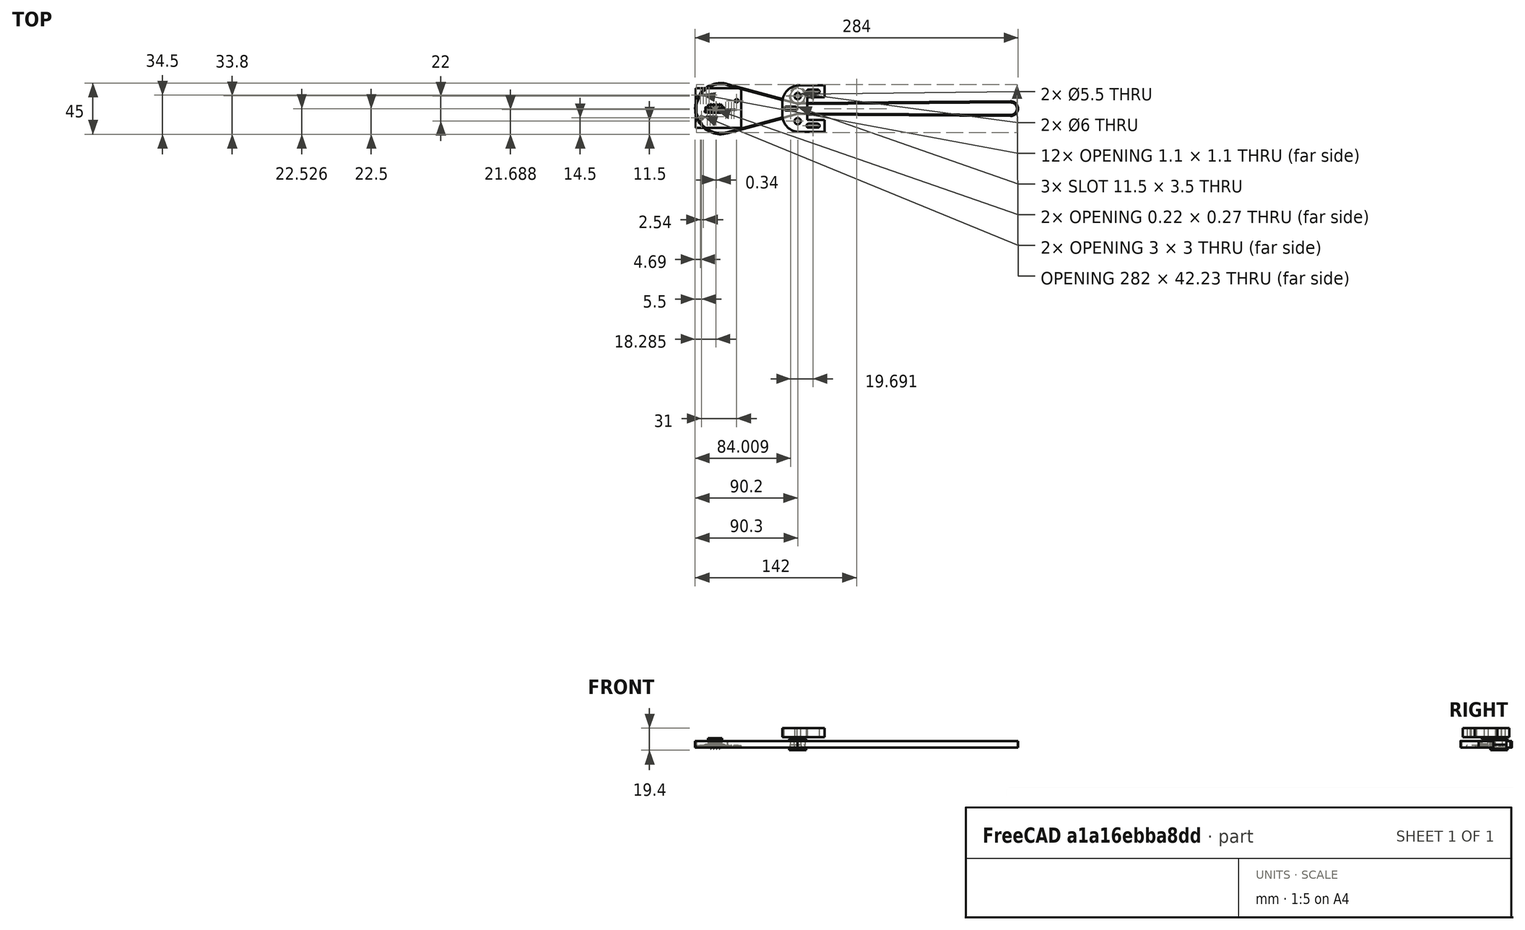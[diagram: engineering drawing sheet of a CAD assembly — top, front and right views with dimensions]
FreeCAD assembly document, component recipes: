
FREECAD ASSEMBLY — COMPONENT RECIPES ("GT2_80")

This assembly document has 18 components, labeled P0..P17 below (a component is one placed body or linked part). 13 of them carry a construction recipe — the FreeCAD feature program that regenerates the part from scratch, quoted from this document or its linked companion documents; the rest are supplied as boundary geometry only. No exploded tour is included for this assembly.
NOTE — document 2 of 2 of this assembly tour. The two overview renders and the header above are repeated from document 1; the component sections below continue where the previous document stopped.
COMPONENT P11 — recipe-attached ("GearHolderFullLength001", modeled in this document).
Construction recipe (the document's own serialized feature program — sketch geometry with constraints, then the solid features built on it; lengths are millimeters unless a unit is written):

FEATURE [PartDesign::ShapeBinder] CopyPocket001
  TraceSupport = false
FEATURE [Sketcher::SketchObject] Sketch079
  ArcFitTolerance = 1e-06
  AttachmentSupport = -> [CopyPocket001]
  FullyConstrained = true
  MakeInternals = false
  MapMode = 5
  Placement = pos=(0,0,19.5) rot=(0,0,1;0rad)
  expr: Constraints[1] = <<Spreadsheet001>>.TopDiameter
  sketch-geometry (1):
    g0: Circle CenterX=0 CenterY=0 CenterZ=0 NormalX=0 NormalY=0 NormalZ=1 AngleXU=0 Radius=32
  constraints (2):
    c: Coincident(g0,g-1)
    c: Diameter(g0) = 64
FEATURE [PartDesign::Pad] Pad033
  Direction = (0,0,1)
  Length = 37
  Length2 = 10
  Profile = -> Sketch079
  ReferenceAxis = -> Sketch079 [N_Axis]
  Refine = true
  Reversed = true
  Suppressed = false
  Type = 0
  expr: Length = <<Spreadsheet001>>.SecondArmHeight
FEATURE [Sketcher::SketchObject] Sketch080
  ArcFitTolerance = 1e-06
  AttachmentSupport = -> [Pad033]
  FullyConstrained = true
  MakeInternals = false
  MapMode = 5
  Placement = pos=(0,0,-17.5) rot=(1,0,0;3.14159rad)
  expr: Constraints[1] = <<Spreadsheet001>>.TopBearingDiameter
  sketch-geometry (1):
    g0: Circle CenterX=0 CenterY=0 CenterZ=0 NormalX=0 NormalY=0 NormalZ=1 AngleXU=0 Radius=18.5
  constraints (2):
    c: Coincident(g0,g-1)
    c: Diameter(g0) = 37
FEATURE [PartDesign::Pocket] Pocket032
  BaseFeature = -> Pad033
  Direction = (0,0,1)
  Length = 35
  Length2 = 5
  Profile = -> Sketch080
  ReferenceAxis = -> Sketch080 [N_Axis]
  Refine = true
  Suppressed = false
  Type = 0
  expr: Length = <<Spreadsheet001>>.SecondArmHeight - <<Spreadsheet001>>.TopThickness
FEATURE [Sketcher::SketchObject] Sketch081
  ArcFitTolerance = 1e-06
  AttachmentSupport = -> [Pocket032]
  FullyConstrained = true
  MakeInternals = false
  MapMode = 5
  Placement = pos=(0,0,-17.5) rot=(1,0,0;3.14159rad)
  expr: Constraints[1] = <<Spreadsheet001>>.TopThrustBearingDiameter + 6
  sketch-geometry (1):
    g0: Circle CenterX=0 CenterY=0 CenterZ=0 NormalX=0 NormalY=0 NormalZ=1 AngleXU=0 Radius=26.5
  constraints (2):
    c: Coincident(g0,g-1)
    c: Diameter(g0) = 53
FEATURE [PartDesign::Pocket] Pocket033
  BaseFeature = -> Pocket032
  Direction = (0,0,1)
  Length = 27
  Length2 = 5
  Profile = -> Sketch081
  ReferenceAxis = -> Sketch081 [N_Axis]
  Refine = true
  Suppressed = false
  Type = 0
  expr: Length = <<Spreadsheet001>>.SecondArmHeight - <<Spreadsheet001>>.TopThickness - <<Spreadsheet001>>.TopBearingHeight
FEATURE [Sketcher::SketchObject] Sketch082
  ArcFitTolerance = 1e-06
  AttachmentSupport = -> [Pocket033]
  FullyConstrained = true
  MakeInternals = false
  MapMode = 5
  Placement = pos=(0,0,19.5) rot=(0,0,1;0rad)
  expr: Constraints[1] = <<Spreadsheet001>>.TopBearingHole + 6
  sketch-geometry (1):
    g0: Circle CenterX=0 CenterY=0 CenterZ=0 NormalX=0 NormalY=0 NormalZ=1 AngleXU=0 Radius=15.5
  constraints (2):
    c: Coincident(g0,g-1)
    c: Diameter(g0) = 31
FEATURE [PartDesign::Pocket] Pocket034
  BaseFeature = -> Pocket033
  Direction = (0,0,-1)
  Length = 5
  Length2 = 5
  Profile = -> Sketch082
  ReferenceAxis = -> Sketch082 [N_Axis]
  Refine = true
  Suppressed = false
  Type = 1
FEATURE [Sketcher::SketchObject] Sketch083
  ArcFitTolerance = 1e-06
  AttachmentSupport = -> [Pocket034]
  FullyConstrained = false
  MakeInternals = false
  MapMode = 5
  Placement = pos=(0,0,19.5) rot=(0,0,1;0rad)
  expr: Constraints[1] = <<Spreadsheet001>>.TopDiameter
  expr: Constraints[7] = (<<Spreadsheet001>>.TopFaceWidth + 4) / 2
  sketch-geometry (5):
    g0: ArcOfCircle CenterX=0 CenterY=0 CenterZ=0 NormalX=0 NormalY=0 NormalZ=1 AngleXU=0 Radius=32 StartAngle=2.13736 EndAngle=4.14582
    g1: LineSegment StartX=-17.1756 StartY=27 StartZ=0 EndX=-230.439 EndY=27 EndZ=0
    g2: LineSegment StartX=-230.439 StartY=-27 StartZ=0 EndX=-17.1756 EndY=-27 EndZ=0
    g3: GeomPoint [constr] X=0 Y=0 Z=0
    g4: ArcOfCircle CenterX=-255 CenterY=0 CenterZ=0 NormalX=0 NormalY=0 NormalZ=1 AngleXU=0 Radius=36.5 StartAngle=0.832663 EndAngle=5.45052
  constraints (13):
    c: Coincident(g0,g-1)
    c: Diameter(g0) = 64
    c: Horizontal(g1)
    c: Horizontal(g2)
    c: Coincident(g3,g0)
    c: Coincident(g1,g0)
    c: Coincident(g2,g0)
    c: Distance(g-1,g1) = 27
    c: PointOnObject(g4,g-1)
    c: Diameter(g4) = 73
    c: DistanceX(g4,g-1) = 255
    c: Coincident(g4,g2)
    c: Coincident(g4,g1)
FEATURE [PartDesign::Pad] Pad034
  BaseFeature = -> Pocket034
  Direction = (0,0,1)
  Length = 37
  Length2 = 10
  Profile = -> Sketch083
  ReferenceAxis = -> Sketch083 [N_Axis]
  Refine = true
  Reversed = true
  Suppressed = false
  Type = 0
  expr: Length = <<Spreadsheet001>>.SecondArmHeight
FEATURE [Sketcher::SketchObject] Sketch084
  ArcFitTolerance = 1e-06
  AttachmentSupport = -> [Pad034]
  ExternalGeometry = -> [Pad034]
  FullyConstrained = false
  MakeInternals = false
  MapMode = 5
  Placement = pos=(0,0,-17.5) rot=(1,0,0;3.14159rad)
  sketch-geometry (6):
    g0: LineSegment StartX=-219.873 StartY=-22 StartZ=0 EndX=-6.4835 EndY=-22 EndZ=0
    g1: LineSegment StartX=-6.4835 StartY=-22 StartZ=0 EndX=-6.4835 EndY=22 EndZ=0
    g2: LineSegment StartX=-6.4835 StartY=22 StartZ=0 EndX=-219.873 EndY=22 EndZ=0
    g3: LineSegment StartX=-219.873 StartY=22 StartZ=0 EndX=-229.114 EndY=15 EndZ=0
    g4: LineSegment StartX=-229.114 StartY=-15 StartZ=0 EndX=-219.873 EndY=-22 EndZ=0
    g5: LineSegment StartX=-229.114 StartY=15 StartZ=0 EndX=-229.114 EndY=-15 EndZ=0
  constraints (14):
    c: Coincident(g0,g1)
    c: Coincident(g1,g2)
    c: Vertical(g1)
    c: Horizontal(g0)
    c: Horizontal(g2)
    c: Distance(g2,g-3) = 5
    c: Distance(g-4,g0) = 5
    c: Coincident(g3,g2)
    c: Coincident(g4,g0)
    c: Vertical(g5)
    c: Coincident(g5,g3)
    c: Coincident(g5,g4)
    c: Distance(g3,g-1) = 15
    c: Distance(g4,g-1) = 15
FEATURE [PartDesign::Pocket] Pocket035
  BaseFeature = -> Pad034
  Direction = (0,0,1)
  Length = 32
  Length2 = 5
  Profile = -> Sketch084
  ReferenceAxis = -> Sketch084 [N_Axis]
  Refine = true
  Suppressed = false
  Type = 0
FEATURE [Sketcher::SketchObject] Sketch085
  ArcFitTolerance = 1e-06
  AttachmentOffset = pos=(0,0,-49) rot=(0,0,1;0rad)
  AttachmentSupport = -> [YZ_Plane015]
  ExternalGeometry = -> [Pocket035]
  FullyConstrained = true
  MakeInternals = false
  MapMode = 5
  Placement = pos=(-49,0,0) rot=(0.57735,0.57735,0.57735;2.0944rad)
  sketch-geometry (5):
    g0: LineSegment StartX=22 StartY=14.5 StartZ=0 EndX=5 EndY=14.5 EndZ=0
    g1: LineSegment StartX=16 StartY=-17.5 StartZ=0 EndX=22 EndY=-17.5 EndZ=0
    g2: LineSegment StartX=22 StartY=-17.5 StartZ=0 EndX=22 EndY=14.5 EndZ=0
    g3: LineSegment StartX=16 StartY=3.5 StartZ=0 EndX=16 EndY=-17.5 EndZ=0
    g4: LineSegment StartX=16 StartY=3.5 StartZ=0 EndX=5 EndY=14.5 EndZ=0
  constraints (13):
    c: Coincident(g-4,g0)
    c: PointOnObject(g1,g-3)
    c: Coincident(g1,g-4)
    c: Coincident(g1,g2)
    c: Coincident(g2,g0)
    c: DistanceX(g1,g1) = 6
    c: Horizontal(g0)
    c: Coincident(g3,g1)
    c: Vertical(g3)
    c: Coincident(g3,g4)
    c: Angle(g4,g3) = 2.35619
    c: DistanceY(g3,g3) = 21
    c: Coincident(g0,g4)
FEATURE [PartDesign::Pad] Pad035
  BaseFeature = -> Pocket035
  Direction = (1,0,0)
  Length = 2
  Length2 = 10
  Profile = -> Sketch085
  ReferenceAxis = -> Sketch085 [N_Axis]
  Refine = true
  Suppressed = false
  Type = 0
FEATURE [PartDesign::Mirrored] Mirrored
  MirrorPlane = -> Sketch085 [V_Axis]
  Refine = true
  Suppressed = false
  TransformMode = 0
FEATURE [PartDesign::LinearPattern] LinearPattern
  Direction = -> X_Axis015
  Length = 150
  Mode = 1
  Occurrences = 4
  Offset = 50
  Refine = true
  Reversed = true
  Suppressed = false
  TransformMode = 0
FEATURE [Sketcher::SketchObject] Sketch086
  ArcFitTolerance = 1e-06
  AttachmentSupport = -> [Pad035]
  ExternalGeometry = -> [Pad035]
  FullyConstrained = true
  MakeInternals = false
  MapMode = 5
  Placement = pos=(0,0,14.5) rot=(1,0,0;3.14159rad)
  sketch-geometry (1):
    g0: Circle CenterX=-48 CenterY=-22 CenterZ=0 NormalX=0 NormalY=0 NormalZ=1 AngleXU=0 Radius=4
  constraints (3):
    c: Diameter(g0) = 8
    c: Horizontal(g0,g-3)
    c: Distance(g0,g-3) = 1
FEATURE [PartDesign::Pad] Pad036
  BaseFeature = -> Pad035
  Direction = (0,0,-1)
  Length = 32
  Length2 = 10
  Profile = -> Sketch086
  ReferenceAxis = -> Sketch086 [N_Axis]
  Refine = true
  Suppressed = false
  Type = 0
FEATURE [Sketcher::SketchObject] Sketch087
  ArcFitTolerance = 1e-06
  AttachmentSupport = -> [Pad036]
  ExternalGeometry = -> [Pad036]
  FullyConstrained = true
  MakeInternals = false
  MapMode = 5
  Placement = pos=(0,0,-17.5) rot=(1,0,0;3.14159rad)
  sketch-geometry (1):
    g0: Circle CenterX=-48 CenterY=-22 CenterZ=0 NormalX=0 NormalY=0 NormalZ=1 AngleXU=0 Radius=2
  constraints (2):
    c: Diameter(g0) = 4
    c: Coincident(g0,g-3)
FEATURE [PartDesign::Pocket] Pocket036
  BaseFeature = -> Pad036
  Direction = (0,0,1)
  Length = 10
  Length2 = 5
  Profile = -> Sketch087
  ReferenceAxis = -> Sketch087 [N_Axis]
  Refine = true
  Suppressed = false
  Type = 0
FEATURE [PartDesign::MultiTransform] MultiTransform
  BaseFeature = -> Pocket036
  Originals = -> [Pad035,Pad036,Pocket036]
  Refine = true
  Suppressed = false
  TransformMode = 0
  Transformations = -> [Mirrored,LinearPattern]
FEATURE [Sketcher::SketchObject] Sketch088
  ArcFitTolerance = 1e-06
  AttachmentSupport = -> [Pocket035]
  ExternalGeometry = -> [Pocket035]
  FullyConstrained = false
  MakeInternals = false
  MapMode = 5
  Placement = pos=(0,0,-17.5) rot=(1,0,0;3.14159rad)
  sketch-geometry (8):
    g0: ArcOfCircle CenterX=-270.556 CenterY=15.5564 CenterZ=0 NormalX=0 NormalY=0 NormalZ=1 AngleXU=0 Radius=6 StartAngle=0.785398 EndAngle=3.92699
    g1: ArcOfCircle CenterX=-239.444 CenterY=15.5563 CenterZ=0 NormalX=0 NormalY=0 NormalZ=1 AngleXU=0 Radius=6 StartAngle=5.49779 EndAngle=8.63938
    g2: ArcOfCircle CenterX=-270.556 CenterY=-15.5564 CenterZ=0 NormalX=0 NormalY=0 NormalZ=1 AngleXU=0 Radius=6 StartAngle=2.35619 EndAngle=5.49779
    g3: ArcOfCircle CenterX=-239.444 CenterY=-15.5563 CenterZ=0 NormalX=0 NormalY=0 NormalZ=1 AngleXU=0 Radius=6 StartAngle=3.92699 EndAngle=7.06858
    g4: ArcOfCircle CenterX=-255 CenterY=0 CenterZ=0 NormalX=0 NormalY=0 NormalZ=1 AngleXU=0 Radius=22.8035 StartAngle=2.62245 EndAngle=3.66074
    g5: ArcOfCircle CenterX=-255 CenterY=0 CenterZ=0 NormalX=0 NormalY=0 NormalZ=1 AngleXU=0 Radius=22.8035 StartAngle=1.05165 EndAngle=2.08994
    g6: ArcOfCircle CenterX=-255 CenterY=0 CenterZ=0 NormalX=0 NormalY=0 NormalZ=1 AngleXU=0 Radius=22.8035 StartAngle=5.76404 EndAngle=6.80233
    g7: ArcOfCircle CenterX=-255 CenterY=0 CenterZ=0 NormalX=0 NormalY=0 NormalZ=1 AngleXU=0 Radius=22.8035 StartAngle=4.19324 EndAngle=5.23154
  constraints (14):
    c: Coincident(g5,g0)
    c: Coincident(g4,g0)
    c: Equal(g4,g5)
    c: Coincident(g4,g5)
    c: Equal(g4,g6)
    c: Coincident(g4,g6)
    c: Coincident(g1,g5)
    c: Coincident(g1,g6)
    c: Coincident(g3,g6)
    c: Coincident(g3,g7)
    c: Equal(g4,g7)
    c: Coincident(g4,g7)
    c: Coincident(g2,g4)
    c: Coincident(g2,g7)
FEATURE [PartDesign::Pocket] Pocket037
  BaseFeature = -> MultiTransform
  Direction = (0,0,1)
  Length = 27
  Length2 = 5
  Profile = -> Sketch088
  ReferenceAxis = -> Sketch088 [N_Axis]
  Refine = true
  Suppressed = false
  Type = 0
FEATURE [Sketcher::SketchObject] Sketch089
  ArcFitTolerance = 1e-06
  AttachmentSupport = -> [Pad034]
  ExternalGeometry = -> [Pad034]
  FullyConstrained = true
  MakeInternals = false
  MapMode = 5
  Placement = pos=(0,0,19.5) rot=(0,0,1;0rad)
  sketch-geometry (5):
    g0: LineSegment StartX=-277 StartY=-22 StartZ=0 EndX=-233 EndY=-22 EndZ=0
    g1: LineSegment StartX=-233 StartY=-22 StartZ=0 EndX=-233 EndY=22 EndZ=0
    g2: LineSegment StartX=-233 StartY=22 StartZ=0 EndX=-277 EndY=22 EndZ=0
    g3: LineSegment StartX=-277 StartY=22 StartZ=0 EndX=-277 EndY=-22 EndZ=0
    g4: GeomPoint [constr] X=-255 Y=0 Z=0
  constraints (12):
    c: Coincident(g0,g1)
    c: Coincident(g1,g2)
    c: Coincident(g2,g3)
    c: Coincident(g3,g0)
    c: Horizontal(g0)
    c: Horizontal(g2)
    c: Vertical(g1)
    c: Vertical(g3)
    c: Symmetric(g2,g0,g4)
    c: Distance(g1,g3) = 44
    c: Distance(g0,g2) = 44
    c: Coincident(g4,g-3)
FEATURE [PartDesign::Pocket] Pocket038
  BaseFeature = -> Pocket037
  Direction = (0,0,-1)
  Length = 7
  Length2 = 5
  Profile = -> Sketch089
  ReferenceAxis = -> Sketch089 [N_Axis]
  Refine = true
  Suppressed = false
  Type = 0
FEATURE [Sketcher::SketchObject] Sketch090
  ArcFitTolerance = 1e-06
  AttachmentSupport = -> [Pad034]
  ExternalGeometry = -> [Pad034]
  FullyConstrained = true
  MakeInternals = false
  MapMode = 5
  Placement = pos=(0,0,19.5) rot=(0,0,1;0rad)
  sketch-geometry (16):
    g0: ArcOfCircle CenterX=-271.5 CenterY=15.5 CenterZ=0 NormalX=0 NormalY=0 NormalZ=1 AngleXU=0 Radius=1.5 StartAngle=1.5708 EndAngle=4.71239
    g1: ArcOfCircle CenterX=-269.5 CenterY=15.5 CenterZ=0 NormalX=0 NormalY=0 NormalZ=1 AngleXU=0 Radius=1.5 StartAngle=4.71239 EndAngle=7.85398
    g2: LineSegment StartX=-271.5 StartY=17 StartZ=0 EndX=-269.5 EndY=17 EndZ=0
    g3: LineSegment StartX=-271.5 StartY=14 StartZ=0 EndX=-269.5 EndY=14 EndZ=0
    g4: ArcOfCircle CenterX=-240.5 CenterY=15.5 CenterZ=0 NormalX=0 NormalY=0 NormalZ=1 AngleXU=0 Radius=1.5 StartAngle=1.5708 EndAngle=4.71239
    g5: ArcOfCircle CenterX=-238.5 CenterY=15.5 CenterZ=0 NormalX=0 NormalY=0 NormalZ=1 AngleXU=0 Radius=1.5 StartAngle=4.71239 EndAngle=7.85398
    g6: LineSegment StartX=-240.5 StartY=17 StartZ=0 EndX=-238.5 EndY=17 EndZ=0
    g7: LineSegment StartX=-240.5 StartY=14 StartZ=0 EndX=-238.5 EndY=14 EndZ=0
    g8: ArcOfCircle CenterX=-271.5 CenterY=-15.5 CenterZ=0 NormalX=0 NormalY=0 NormalZ=1 AngleXU=0 Radius=1.5 StartAngle=1.5708 EndAngle=4.71239
    g9: ArcOfCircle CenterX=-269.5 CenterY=-15.5 CenterZ=0 NormalX=0 NormalY=0 NormalZ=1 AngleXU=0 Radius=1.5 StartAngle=4.71239 EndAngle=7.85398
    g10: LineSegment StartX=-271.5 StartY=-14 StartZ=0 EndX=-269.5 EndY=-14 EndZ=0
    g11: LineSegment StartX=-271.5 StartY=-17 StartZ=0 EndX=-269.5 EndY=-17 EndZ=0
    g12: ArcOfCircle CenterX=-240.5 CenterY=-15.5 CenterZ=0 NormalX=0 NormalY=0 NormalZ=1 AngleXU=0 Radius=1.5 StartAngle=1.5708 EndAngle=4.71239
    g13: ArcOfCircle CenterX=-238.5 CenterY=-15.5 CenterZ=0 NormalX=0 NormalY=0 NormalZ=1 AngleXU=0 Radius=1.5 StartAngle=4.71239 EndAngle=7.85398
    g14: LineSegment StartX=-240.5 StartY=-14 StartZ=0 EndX=-238.5 EndY=-14 EndZ=0
    g15: LineSegment StartX=-240.5 StartY=-17 StartZ=0 EndX=-238.5 EndY=-17 EndZ=0
  constraints (40):
    c: Tangent(g0,g2) = 1.5708
    c: Tangent(g0,g3) = -1.5708
    c: Tangent(g1,g2) = 1.5708
    c: Tangent(g1,g3) = -1.5708
    c: Equal(g0,g1)
    c: Horizontal(g3)
    c: Radius(g0) = 1.5
    c: Tangent(g4,g6) = 1.5708
    c: Tangent(g4,g7) = -1.5708
    c: Tangent(g5,g6) = 1.5708
    c: Tangent(g5,g7) = -1.5708
    c: Equal(g4,g5)
    c: Radius(g4) = 1.5
    c: Horizontal(g6)
    c: DistanceX(g2,g2) = 2
    c: DistanceX(g6,g6) = 2
    c: Tangent(g8,g10) = 1.5708
    c: Tangent(g8,g11) = -1.5708
    c: Tangent(g9,g10) = 1.5708
    c: Tangent(g9,g11) = -1.5708
    c: Equal(g8,g9)
    c: Horizontal(g11)
    c: Distance(g8,g9) = 2
    c: Radius(g8) = 1.5
    c: Tangent(g12,g14) = 1.5708
    c: Tangent(g12,g15) = -1.5708
    c: Tangent(g13,g14) = 1.5708
    c: Tangent(g13,g15) = -1.5708
    c: Equal(g12,g13)
    c: Horizontal(g15)
    c: Distance(g12,g13) = 2
    c: Radius(g12) = 1.5
    c: Distance(g12,g-1) = 15.5
    c: Distance(g5,g-1) = 15.5
    c: Distance(g1,g-1) = 15.5
    c: Distance(g9,g-1) = 15.5
    c: DistanceX(g1,g-3) = 14.5
    c: DistanceX(g-3,g4) = 14.5
    c: DistanceX(g-3,g12) = 14.5
    c: DistanceX(g9,g-3) = 14.5
FEATURE [PartDesign::Pocket] Pocket039
  BaseFeature = -> Pocket038
  Direction = (0,0,-1)
  Length = 5
  Length2 = 5
  Profile = -> Sketch090
  ReferenceAxis = -> Sketch090 [N_Axis]
  Refine = true
  Suppressed = false
  Type = 1
FEATURE [Sketcher::SketchObject] Sketch091
  ArcFitTolerance = 1e-06
  AttachmentSupport = -> [Pocket039]
  ExternalGeometry = -> [Pocket039]
  FullyConstrained = false
  MakeInternals = false
  MapMode = 5
  Placement = pos=(0,0,19.5) rot=(0,0,1;0rad)
  sketch-geometry (4):
    g0: ArcOfCircle CenterX=-287 CenterY=0 CenterZ=0 NormalX=0 NormalY=0 NormalZ=1 AngleXU=0 Radius=4 StartAngle=4.71239 EndAngle=7.85398
    g1: ArcOfCircle CenterX=-304.496 CenterY=1.02e-14 CenterZ=0 NormalX=0 NormalY=0 NormalZ=1 AngleXU=0 Radius=4 StartAngle=1.5708 EndAngle=4.71239
    g2: LineSegment StartX=-287 StartY=-4 StartZ=0 EndX=-304.496 EndY=-4 EndZ=0
    g3: LineSegment StartX=-287 StartY=4 StartZ=0 EndX=-304.496 EndY=4 EndZ=0
  constraints (9):
    c: Tangent(g0,g2) = 1.5708
    c: Tangent(g0,g3) = -1.5708
    c: Tangent(g1,g2) = 1.5708
    c: Tangent(g1,g3) = -1.5708
    c: Equal(g0,g1)
    c: Horizontal(g3)
    c: Radius(g0) = 4
    c: PointOnObject(g0,g-1)
    c: DistanceX(g0,g-3) = 32
FEATURE [PartDesign::Pocket] Pocket040
  BaseFeature = -> Pocket039
  Direction = (0,0,-1)
  Length = 32
  Length2 = 5
  Profile = -> Sketch091
  ReferenceAxis = -> Sketch091 [N_Axis]
  Refine = true
  Suppressed = false
  Type = 0
FEATURE [PartDesign::Line] DatumLine
  AttacherType = Attacher::AttachEngineLine
  AttachmentOffset = pos=(-255,0,0) rot=(0,0,1;0rad)
  AttachmentSupport = -> [Z_Axis015]
  Length = 20
  MapMode = 29
  Placement = pos=(-255,0,0) rot=(0,0,1;0rad)
  ResizeMode = 0
FEATURE [PartDesign::PolarPattern] PolarPattern006
  Angle = 360
  Axis = -> DatumLine
  Mode = 1
  Occurrences = 3
  Offset = 60
  Refine = true
  Reversed = true
  Suppressed = false
  TransformMode = 0
FEATURE [PartDesign::PolarPattern] PolarPattern007
  Angle = 360
  Axis = -> DatumLine
  Mode = 1
  Occurrences = 3
  Offset = 60
  Refine = true
  Suppressed = false
  TransformMode = 0
FEATURE [PartDesign::Pocket] Pocket043
  BaseFeature = -> Pocket040
  Direction = (0,0,-1)
  Length = 5
  Length2 = 5
  Profile = -> Sketch094
  ReferenceAxis = -> Sketch094 [N_Axis]
  Refine = true
  Suppressed = false
  Type = 1
FEATURE [PartDesign::MultiTransform] MultiTransform001
  BaseFeature = -> Pocket043
  Originals = -> [Pocket040,Pocket043]
  Refine = true
  Suppressed = false
  TransformMode = 0
  Transformations = -> [PolarPattern006,PolarPattern007]
FEATURE [Sketcher::SketchObject] Sketch092
  ArcFitTolerance = 1e-06
  AttachmentSupport = -> [MultiTransform001]
  FullyConstrained = false
  MakeInternals = false
  MapMode = 5
  Placement = pos=(0,0,-17.5) rot=(1,0,0;3.14159rad)
  sketch-geometry (4):
    g0: LineSegment StartX=-249.696 StartY=15 StartZ=0 EndX=-249.696 EndY=-15 EndZ=0
    g1: LineSegment StartX=-249.696 StartY=-15 StartZ=0 EndX=-214.114 EndY=-15 EndZ=0
    g2: LineSegment StartX=-214.114 StartY=-15 StartZ=0 EndX=-214.114 EndY=15 EndZ=0
    g3: LineSegment StartX=-214.114 StartY=15 StartZ=0 EndX=-249.696 EndY=15 EndZ=0
  constraints (10):
    c: Coincident(g0,g1)
    c: Coincident(g1,g2)
    c: Coincident(g2,g3)
    c: Coincident(g3,g0)
    c: Vertical(g0)
    c: Vertical(g2)
    c: Horizontal(g1)
    c: Horizontal(g3)
    c: Distance(g-1,g3) = 15
    c: Distance(g1,g-1) = 15
FEATURE [PartDesign::Pocket] Pocket041
  BaseFeature = -> MultiTransform001
  Direction = (0,0,1)
  Length = 27
  Length2 = 5
  Profile = -> Sketch092
  ReferenceAxis = -> Sketch092 [N_Axis]
  Refine = true
  Suppressed = false
  Type = 0
FEATURE [Sketcher::SketchObject] Sketch093
  ArcFitTolerance = 1e-06
  AttachmentSupport = -> [Pocket041]
  FullyConstrained = true
  MakeInternals = false
  MapMode = 5
  Placement = pos=(0,0,9.5) rot=(1,0,0;3.14159rad)
  sketch-geometry (1):
    g0: Circle CenterX=-255 CenterY=0 CenterZ=0 NormalX=0 NormalY=0 NormalZ=1 AngleXU=0 Radius=15
  constraints (2):
    c: Diameter(g0) = 30
    c: Coincident(g0,g-3)
FEATURE [PartDesign::Body] Body008  label="GearHolderFullLength"
  AllowCompound = false
  Group = -> [CopyPocket001,Sketch079,Pad033,Sketch080,Pocket032,Sketch081,Pocket033,Sketch082,Pocket034,Sketch083,Pad034,Sketch084,Pocket035,Sketch085,Pad035,Mirrored,LinearPattern,Sketch086,Pad036,Sketch087,Pocket036,MultiTransform,Sketch088,Pocket037,Sketch089,Pocket038,Sketch090,Pocket039,Sketch091,Pocket040,Pocket043,DatumLine,MultiTransform001,PolarPattern006,PolarPattern007,Sketch092,Pocket041,Sketch093,+7 more]
  Origin = -> Origin015
  Placement = pos=(5,-1.19209e-06,2.46221) rot=(0,0,1;3.14159rad)
  Tip = -> Pocket046
COMPONENT P12 — recipe-attached ("F686zzBottom", modeled in this document).
Construction recipe (the document's own serialized feature program — sketch geometry with constraints, then the solid features built on it; lengths are millimeters unless a unit is written):

FEATURE [PartDesign::ShapeBinder] CopyPocket
  TraceSupport = false
FEATURE [Sketcher::SketchObject] Sketch025
  ArcFitTolerance = 1e-06
  AttachmentSupport = -> [CopyPocket]
  FullyConstrained = true
  MakeInternals = false
  MapMode = 5
  Placement = pos=(0,0,19.5) rot=(0,0,1;0rad)
  expr: Constraints[1] = <<Spreadsheet>>.TopDiameter
  sketch-geometry (1):
    g0: Circle CenterX=0 CenterY=0 CenterZ=0 NormalX=0 NormalY=0 NormalZ=1 AngleXU=0 Radius=32
  constraints (2):
    c: Coincident(g0,g-1)
    c: Diameter(g0) = 64
FEATURE [PartDesign::Pad] Pad016
  Direction = (0,0,1)
  Length = 37
  Length2 = 10
  Profile = -> Sketch025
  ReferenceAxis = -> Sketch025 [N_Axis]
  Refine = true
  Reversed = true
  Suppressed = false
  Type = 0
  expr: Length = <<Spreadsheet>>.SecondArmHeight
FEATURE [Sketcher::SketchObject] Sketch026
  ArcFitTolerance = 1e-06
  AttachmentSupport = -> [Pad016]
  FullyConstrained = true
  MakeInternals = false
  MapMode = 5
  Placement = pos=(0,0,-17.5) rot=(1,0,0;3.14159rad)
  expr: Constraints[1] = <<Spreadsheet>>.TopBearingDiameter
  sketch-geometry (1):
    g0: Circle CenterX=0 CenterY=0 CenterZ=0 NormalX=0 NormalY=0 NormalZ=1 AngleXU=0 Radius=18.5
  constraints (2):
    c: Coincident(g0,g-1)
    c: Diameter(g0) = 37
FEATURE [PartDesign::Pocket] Pocket001
  BaseFeature = -> Pad016
  Direction = (0,0,1)
  Length = 35
  Length2 = 5
  Profile = -> Sketch026
  ReferenceAxis = -> Sketch026 [N_Axis]
  Refine = true
  Suppressed = false
  Type = 0
  expr: Length = <<Spreadsheet>>.SecondArmHeight - <<Spreadsheet>>.TopThickness
FEATURE [Sketcher::SketchObject] Sketch027
  ArcFitTolerance = 1e-06
  AttachmentSupport = -> [Pocket001]
  FullyConstrained = true
  MakeInternals = false
  MapMode = 5
  Placement = pos=(0,0,-17.5) rot=(1,0,0;3.14159rad)
  expr: Constraints[1] = <<Spreadsheet>>.TopThrustBearingDiameter + 6
  sketch-geometry (1):
    g0: Circle CenterX=0 CenterY=0 CenterZ=0 NormalX=0 NormalY=0 NormalZ=1 AngleXU=0 Radius=26.5
  constraints (2):
    c: Coincident(g0,g-1)
    c: Diameter(g0) = 53
FEATURE [PartDesign::Pocket] Pocket002
  BaseFeature = -> Pocket001
  Direction = (0,0,1)
  Length = 27
  Length2 = 5
  Profile = -> Sketch027
  ReferenceAxis = -> Sketch027 [N_Axis]
  Refine = true
  Suppressed = false
  Type = 0
  expr: Length = <<Spreadsheet>>.SecondArmHeight - <<Spreadsheet>>.TopThickness - <<Spreadsheet>>.TopBearingHeight
FEATURE [Sketcher::SketchObject] Sketch028
  ArcFitTolerance = 1e-06
  AttachmentSupport = -> [Pocket002]
  FullyConstrained = true
  MakeInternals = false
  MapMode = 5
  Placement = pos=(0,0,19.5) rot=(0,0,1;0rad)
  expr: Constraints[1] = <<Spreadsheet>>.TopBearingHole + 6
  sketch-geometry (1):
    g0: Circle CenterX=0 CenterY=0 CenterZ=0 NormalX=0 NormalY=0 NormalZ=1 AngleXU=0 Radius=15.5
  constraints (2):
    c: Coincident(g0,g-1)
    c: Diameter(g0) = 31
FEATURE [PartDesign::Pocket] Pocket003
  BaseFeature = -> Pocket002
  Direction = (0,0,-1)
  Length = 5
  Length2 = 5
  Profile = -> Sketch028
  ReferenceAxis = -> Sketch028 [N_Axis]
  Refine = true
  Suppressed = false
  Type = 1
FEATURE [Sketcher::SketchObject] Sketch030
  ArcFitTolerance = 1e-06
  AttachmentSupport = -> [Pocket003]
  FullyConstrained = true
  MakeInternals = false
  MapMode = 5
  Placement = pos=(0,0,19.5) rot=(0,0,1;0rad)
  expr: Constraints[10] = <<Spreadsheet>>.TopFaceSize
  expr: Constraints[11] = <<Spreadsheet>>.TopFaceWidth + 4
  expr: Constraints[12] = (<<Spreadsheet>>.TopFaceWidth + 4) / 2
  expr: Constraints[1] = <<Spreadsheet>>.TopDiameter
  sketch-geometry (5):
    g0: ArcOfCircle CenterX=0 CenterY=0 CenterZ=0 NormalX=0 NormalY=0 NormalZ=1 AngleXU=0 Radius=32 StartAngle=2.13736 EndAngle=4.14582
    g1: LineSegment StartX=-17.1756 StartY=27 StartZ=0 EndX=-200 EndY=27 EndZ=0
    g2: LineSegment StartX=-200 StartY=27 StartZ=0 EndX=-200 EndY=-27 EndZ=0
    g3: LineSegment StartX=-200 StartY=-27 StartZ=0 EndX=-17.1756 EndY=-27 EndZ=0
    g4: GeomPoint [constr] X=0 Y=0 Z=0
  constraints (13):
    c: Coincident(g0,g-1)
    c: Diameter(g0) = 64
    c: Coincident(g1,g2)
    c: Coincident(g2,g3)
    c: Vertical(g2)
    c: Horizontal(g1)
    c: Horizontal(g3)
    c: Coincident(g4,g0)
    c: Coincident(g1,g0)
    c: Coincident(g3,g0)
    c: Distance(g-2,g2) = 200
    c: DistanceY(g2,g2) = 54
    c: Distance(g-1,g1) = 27
FEATURE [PartDesign::Pad] Pad018
  BaseFeature = -> Pocket003
  Direction = (0,0,1)
  Length = 37
  Length2 = 10
  Profile = -> Sketch030
  ReferenceAxis = -> Sketch030 [N_Axis]
  Refine = true
  Reversed = true
  Suppressed = false
  Type = 0
  expr: Length = <<Spreadsheet>>.SecondArmHeight
FEATURE [Sketcher::SketchObject] Sketch034
  ArcFitTolerance = 1e-06
  AttachmentSupport = -> [Pad018]
  FullyConstrained = true
  MakeInternals = false
  MapMode = 5
  Placement = pos=(-200,0,0) rot=(0.57735,-0.57735,-0.57735;2.0944rad)
  expr: Constraints[10] = <<Spreadsheet>>.CuroaHoleSize / 2
  expr: Constraints[11] = <<Spreadsheet>>.CuroaHoleSize / 2
  sketch-geometry (4):
    g0: LineSegment StartX=-20 StartY=14.5 StartZ=0 EndX=-20 EndY=-17.5 EndZ=0
    g1: LineSegment StartX=-20 StartY=-17.5 StartZ=0 EndX=20 EndY=-17.5 EndZ=0
    g2: LineSegment StartX=20 StartY=-17.5 StartZ=0 EndX=20 EndY=14.5 EndZ=0
    g3: LineSegment StartX=20 StartY=14.5 StartZ=0 EndX=-20 EndY=14.5 EndZ=0
  constraints (12):
    c: Coincident(g0,g1)
    c: Coincident(g1,g2)
    c: Coincident(g2,g3)
    c: Coincident(g3,g0)
    c: Vertical(g0)
    c: Vertical(g2)
    c: Horizontal(g1)
    c: Horizontal(g3)
    c: PointOnObject(g0,g-3)
    c: PointOnObject(g1,g-4)
    c: Distance(g-2,g0) = 20
    c: Distance(g-2,g2) = 20
FEATURE [PartDesign::Pocket] Pocket004
  BaseFeature = -> Pad018
  Direction = (1,0,0)
  Length = 200
  Length2 = 5
  Profile = -> Sketch034
  ReferenceAxis = -> Sketch034 [N_Axis]
  Refine = true
  Suppressed = false
  Type = 0
  expr: Length = <<Spreadsheet>>.TopFaceSize
FEATURE [Sketcher::SketchObject] Sketch046
  ArcFitTolerance = 1e-06
  AttachmentSupport = -> [Pocket004]
  ExternalGeometry = -> [Pocket004]
  FullyConstrained = true
  MakeInternals = false
  MapMode = 5
  Placement = pos=(-200,0,0) rot=(0.57735,-0.57735,-0.57735;2.0944rad)
  expr: Constraints[10] = <<Spreadsheet>>.TopFaceWidth + 4
  expr: Constraints[12] = <<Spreadsheet>>.SecondArmHeight
  sketch-geometry (11):
    g0: LineSegment StartX=27 StartY=-17.5 StartZ=0 EndX=27 EndY=19.5 EndZ=0
    g1: LineSegment StartX=27 StartY=19.5 StartZ=0 EndX=-27 EndY=19.5 EndZ=0
    g2: LineSegment StartX=-27 StartY=19.5 StartZ=0 EndX=-27 EndY=-17.5 EndZ=0
    g3: LineSegment StartX=-27 StartY=-17.5 StartZ=0 EndX=27 EndY=-17.5 EndZ=0
    g4: GeomPoint [constr] X=0 Y=1 Z=0
    g5: GeomPoint [constr] X=0 Y=1 Z=0
    g6: LineSegment StartX=9 StartY=-8.5 StartZ=0 EndX=9 EndY=6.5 EndZ=0
    g7: LineSegment StartX=9 StartY=6.5 StartZ=0 EndX=-9 EndY=6.5 EndZ=0
    g8: LineSegment StartX=-9 StartY=6.5 StartZ=0 EndX=-9 EndY=-8.5 EndZ=0
    g9: LineSegment StartX=-9 StartY=-8.5 StartZ=0 EndX=9 EndY=-8.5 EndZ=0
    g10: GeomPoint [constr] X=0 Y=-1 Z=0
  constraints (27):
    c: Coincident(g0,g1)
    c: Coincident(g1,g2)
    c: Coincident(g2,g3)
    c: Coincident(g3,g0)
    c: Vertical(g0)
    c: Vertical(g2)
    c: Horizontal(g1)
    c: Horizontal(g3)
    c: Symmetric(g2,g0,g4)
    c: PointOnObject(g4,g-2)
    c: DistanceX(g3,g3) = 54
    c: Distance(g4,g-3) = 18.5
    c: DistanceY(g0,g0) = 37
    c: Coincident(g5,g4)
    c: Coincident(g6,g7)
    c: Coincident(g7,g8)
    c: Coincident(g8,g9)
    c: Coincident(g9,g6)
    c: Vertical(g6)
    c: Vertical(g8)
    c: Horizontal(g7)
    c: Horizontal(g9)
    c: Symmetric(g8,g6,g10)
    c: PointOnObject(g10,g-2)
    c: Distance(g10,g3) = 16.5
    c: DistanceY(g6,g6) = 15
    c: DistanceX(g7,g7) = 18
FEATURE [PartDesign::Pad] Pad020
  BaseFeature = -> Pocket004
  Direction = (-1,0,0)
  Length = 10
  Length2 = 10
  Profile = -> Sketch046
  ReferenceAxis = -> Sketch046 [N_Axis]
  Refine = true
  Suppressed = false
  Type = 0
FEATURE [Sketcher::SketchObject] Sketch047
  ArcFitTolerance = 1e-06
  AttachmentSupport = -> [Pad020]
  FullyConstrained = true
  MakeInternals = false
  MapMode = 5
  Placement = pos=(0,0,-17.5) rot=(1,0,0;3.14159rad)
  sketch-geometry (1):
    g0: Circle CenterX=29.53 CenterY=0 CenterZ=0 NormalX=0 NormalY=0 NormalZ=1 AngleXU=0 Radius=1.5
  constraints (3):
    c: PointOnObject(g0,g-1)
    c: DistanceX(g-1,g0) = 29.53
    c: Diameter(g0) = 3
FEATURE [PartDesign::Pocket] Pocket
  BaseFeature = -> Pad020
  Direction = (0,0,1)
  Length = 10
  Length2 = 5
  Profile = -> Sketch047
  ReferenceAxis = -> Sketch047 [N_Axis]
  Refine = true
  Suppressed = false
  Type = 0
FEATURE [PartDesign::PolarPattern] PolarPattern003
  Angle = 360
  Axis = -> Sketch047 [N_Axis]
  BaseFeature = -> Pocket
  Mode = 0
  Occurrences = 3
  Offset = 120
  Originals = -> [Pocket]
  Refine = true
  Suppressed = false
  TransformMode = 0
FEATURE [PartDesign::Chamfer] Chamfer002
  Angle = 45
  Base = -> PolarPattern003 [Edge2,Edge5]
  BaseFeature = -> PolarPattern003
  ChamferType = 0
  FlipDirection = false
  Refine = true
  Size = 5
  Size2 = 1
  SupportTransform = false
  Suppressed = false
  UseAllEdges = false
FEATURE [Sketcher::SketchObject] Sketch063
  ArcFitTolerance = 1e-06
  AttachmentSupport = -> [Chamfer002]
  FullyConstrained = true
  MakeInternals = false
  MapMode = 5
  Placement = pos=(-200,0,0) rot=(0.57735,0.57735,0.57735;2.0944rad)
  sketch-geometry (4):
    g0: Circle CenterX=-14 CenterY=4.5 CenterZ=0 NormalX=0 NormalY=0 NormalZ=1 AngleXU=0 Radius=2.5
    g1: Circle CenterX=14 CenterY=4.5 CenterZ=0 NormalX=0 NormalY=0 NormalZ=1 AngleXU=0 Radius=2.5
    g2: Circle CenterX=-14 CenterY=-10 CenterZ=0 NormalX=0 NormalY=0 NormalZ=1 AngleXU=0 Radius=2.5
    g3: Circle CenterX=14 CenterY=-10 CenterZ=0 NormalX=0 NormalY=0 NormalZ=1 AngleXU=0 Radius=2.5
  constraints (12):
    c: Diameter(g0) = 5
    c: Diameter(g1) = 5
    c: Diameter(g2) = 5
    c: Diameter(g3) = 5
    c: Distance(g0,g-1) = 4.5
    c: DistanceX(g0,g-1) = 14
    c: Horizontal(g1,g0)
    c: Vertical(g1,g3)
    c: Vertical(g0,g2)
    c: Horizontal(g2,g3)
    c: Distance(g3,g-1) = 10
    c: DistanceX(g-1,g1) = 14
FEATURE [PartDesign::Pocket] Pocket022
  BaseFeature = -> Chamfer002
  Direction = (-1,0,0)
  Length = 5
  Length2 = 5
  Profile = -> Sketch063
  ReferenceAxis = -> Sketch063 [N_Axis]
  Refine = true
  Suppressed = false
  Type = 1
FEATURE [PartDesign::Body] Body  label="GearHolder"
  AllowCompound = false
  Group = -> [CopyPocket,Sketch025,Pad016,Sketch026,Pocket001,Sketch027,Pocket002,Sketch028,Pocket003,Sketch030,Pad018,Sketch034,Pocket004,Sketch046,Pad020,Sketch047,Pocket,PolarPattern003,Chamfer002,Sketch063,Pocket022]
  Origin = -> Origin
  Placement = pos=(5,-1.19209e-06,2.46221) rot=(0,0,1;3.14159rad)
  Tip = -> Pocket022
COMPONENT P13 — same part as P12; its construction recipe is shown at P12.
COMPONENT P14 — geometry summary ("FastenBelt001"; no construction recipe available for this part):
  bounding box: 284.0 x 45.0 x 19.4 mm
  tessellated surface: 9,600 triangles
  volume: 13595 mm^3 (5% of its bounding box)
  symmetry: mirror-symmetric across its y mid-plane
COMPONENT P15 — geometry summary ("MainArmRotatorV003"; no construction recipe available for this part):
  bounding box: 73.0 x 73.0 x 5.0 mm
  tessellated surface: 5,304 triangles
  volume: 17259 mm^3 (65% of its bounding box)
  symmetry: 2-fold rotationally symmetric about the x axis; 2-fold rotationally symmetric about the y axis; 6-fold rotationally symmetric about the z axis; mirror-symmetric across its x mid-plane, z mid-plane
COMPONENT P16 — recipe-attached ("MainArmCover001", modeled in this document).
Construction recipe (the document's own serialized feature program — sketch geometry with constraints, then the solid features built on it; lengths are millimeters unless a unit is written):

FEATURE [Sketcher::SketchObject] Sketch098
  ArcFitTolerance = 1e-06
  AttachmentSupport = -> [XY_Plane018]
  FullyConstrained = false
  MakeInternals = false
  MapMode = 5
  sketch-geometry (8):
    g0: LineSegment StartX=18.0901 StartY=-27 StartZ=0 EndX=229.702 EndY=-27 EndZ=0
    g1: LineSegment StartX=229.702 StartY=27 StartZ=0 EndX=18.0901 EndY=27 EndZ=0
    g2: ArcOfCircle CenterX=0 CenterY=0 CenterZ=0 NormalX=0 NormalY=0 NormalZ=1 AngleXU=0 Radius=32.5 StartAngle=5.3027 EndAngle=5.58065
    g3: ArcOfCircle CenterX=18 CenterY=0 CenterZ=0 NormalX=0 NormalY=0 NormalZ=1 AngleXU=0 Radius=28 StartAngle=5.43512 EndAngle=7.13125
    g4: LineSegment StartX=36.5203 StartY=-21 StartZ=0 EndX=24.8042 EndY=-21 EndZ=0
    g5: LineSegment StartX=36.5203 StartY=21 StartZ=0 EndX=24.8042 EndY=21 EndZ=0
    g6: ArcOfCircle CenterX=0 CenterY=0 CenterZ=0 NormalX=0 NormalY=0 NormalZ=1 AngleXU=0 Radius=32.5 StartAngle=0.702534 EndAngle=0.980488
    g7: ArcOfCircle CenterX=255 CenterY=0 CenterZ=0 NormalX=0 NormalY=0 NormalZ=1 AngleXU=0 Radius=37 StartAngle=2.32367 EndAngle=3.95952
  constraints (25):
    c: Horizontal(g0)
    c: Horizontal(g1)
    c: Distance(g-1,g0) = 27
    c: Distance(g-1,g1) = 27
    c: Diameter(g2) = 65
    c: Coincident(g2,g-1)
    c: PointOnObject(g3,g-1)
    c: DistanceX(g-1,g3) = 18
    c: Radius(g3) = 28
    c: Coincident(g4,g3)
    c: Horizontal(g4)
    c: Coincident(g5,g3)
    c: PointOnObject(g5,g6)
    c: Horizontal(g5)
    c: Equal(g2,g6)
    c: Coincident(g2,g4)
    c: PointOnObject(g6,g5)
    c: Coincident(g2,g6)
    c: Coincident(g1,g6)
    c: Coincident(g0,g2)
    c: Diameter(g7) = 74
    c: PointOnObject(g7,g-1)
    c: DistanceX(g-1,g7) = 255
    c: Coincident(g7,g0)
    c: Coincident(g1,g7)
FEATURE [PartDesign::Pad] Pad039
  Direction = (0,0,1)
  Length = 5
  Length2 = 10
  Profile = -> Sketch098
  ReferenceAxis = -> Sketch098 [N_Axis]
  Refine = true
  Suppressed = false
  Type = 0
FEATURE [Sketcher::SketchObject] Sketch099
  ArcFitTolerance = 1e-06
  AttachmentSupport = -> [Pad039]
  ExternalGeometry = -> [Pad039]
  FullyConstrained = true
  MakeInternals = false
  MapMode = 5
  Placement = pos=(0,0,0) rot=(1,0,0;3.14159rad)
  sketch-geometry (2):
    g0: Circle CenterX=48 CenterY=22 CenterZ=0 NormalX=0 NormalY=0 NormalZ=1 AngleXU=0 Radius=1.5
    g1: Circle CenterX=48 CenterY=-22 CenterZ=0 NormalX=0 NormalY=0 NormalZ=1 AngleXU=0 Radius=1.5
  constraints (6):
    c: Diameter(g0) = 3
    c: Diameter(g1) = 3
    c: Distance(g0,g-3) = 5
    c: Distance(g1,g-4) = 5
    c: Vertical(g0,g1)
    c: DistanceX(g-1,g0) = 48
FEATURE [PartDesign::Thickness] Thickness001
  Base = -> Pad039 [Face10]
  BaseFeature = -> Pad039
  Intersection = true
  Join = 0
  Mode = 0
  Refine = true
  Reversed = true
  SupportTransform = false
  Suppressed = false
  Value = 1.5
FEATURE [PartDesign::Pocket] Pocket045
  BaseFeature = -> Thickness001
  Direction = (0,0,1)
  Length = 5
  Length2 = 5
  Profile = -> Sketch099
  ReferenceAxis = -> Sketch099 [N_Axis]
  Refine = true
  Suppressed = false
  Type = 0
FEATURE [Sketcher::SketchObject] Sketch100
  ArcFitTolerance = 1e-06
  AttachmentSupport = -> [Pocket045]
  ExternalGeometry = -> [Pocket045]
  FullyConstrained = true
  MakeInternals = false
  MapMode = 5
  Placement = pos=(0,0,1.5) rot=(0,0,1;0rad)
  sketch-geometry (10):
    g0: Circle CenterX=48 CenterY=22 CenterZ=0 NormalX=0 NormalY=0 NormalZ=1 AngleXU=0 Radius=1.5
    g1: ArcOfCircle CenterX=48 CenterY=22 CenterZ=0 NormalX=0 NormalY=0 NormalZ=1 AngleXU=0 Radius=3 StartAngle=3.14159 EndAngle=6.28319
    g2: Circle CenterX=48 CenterY=-22 CenterZ=0 NormalX=0 NormalY=0 NormalZ=1 AngleXU=0 Radius=1.5
    g3: ArcOfCircle CenterX=48 CenterY=-22 CenterZ=0 NormalX=0 NormalY=0 NormalZ=1 AngleXU=0 Radius=3 StartAngle=0 EndAngle=3.14159
    g4: LineSegment StartX=45 StartY=25.5 StartZ=0 EndX=45 EndY=22 EndZ=0
    g5: LineSegment StartX=51 StartY=22 StartZ=0 EndX=51 EndY=25.5 EndZ=0
    g6: LineSegment StartX=45 StartY=25.5 StartZ=0 EndX=51 EndY=25.5 EndZ=0
    g7: LineSegment StartX=45 StartY=-22 StartZ=0 EndX=45 EndY=-25.5 EndZ=0
    g8: LineSegment StartX=51 StartY=-22 StartZ=0 EndX=51 EndY=-25.5 EndZ=0
    g9: LineSegment StartX=45 StartY=-25.5 StartZ=0 EndX=51 EndY=-25.5 EndZ=0
  constraints (25):
    c: Coincident(g0,g-3)
    c: Equal(g0,g-3)
    c: Diameter(g1) = 6
    c: Coincident(g1,g0)
    c: Coincident(g2,g-4)
    c: Equal(g2,g-4)
    c: Diameter(g3) = 6
    c: Coincident(g3,g2)
    c: PointOnObject(g4,g-5)
    c: PointOnObject(g5,g-5)
    c: Vertical(g5)
    c: Vertical(g4)
    c: Distance(g0,g5) = 3
    c: Coincident(g4,g6)
    c: Coincident(g6,g5)
    c: Coincident(g1,g5)
    c: Tangent(g1,g4) = -1.5708
    c: PointOnObject(g7,g-6)
    c: PointOnObject(g8,g-6)
    c: Vertical(g8)
    c: Vertical(g7)
    c: Coincident(g9,g7)
    c: Coincident(g9,g8)
    c: Tangent(g3,g7) = -1.5708
    c: Tangent(g3,g8) = 1.5708
FEATURE [PartDesign::Pad] Pad040
  BaseFeature = -> Pocket045
  Direction = (0,0,1)
  Length = 3
  Length2 = 10
  Profile = -> Sketch100
  ReferenceAxis = -> Sketch100 [N_Axis]
  Refine = true
  Suppressed = false
  Type = 0
FEATURE [PartDesign::LinearPattern] LinearPattern001
  BaseFeature = -> Pad040
  Direction = -> Sketch099 [H_Axis]
  Length = 150
  Mode = 1
  Occurrences = 4
  Offset = 50
  Originals = -> [Pocket045,Pad040]
  Refine = true
  Suppressed = false
  TransformMode = 0
FEATURE [Sketcher::SketchObject] Sketch102
  ArcFitTolerance = 1e-06
  AttachmentSupport = -> [LinearPattern001]
  FullyConstrained = false
  MakeInternals = false
  MapMode = 5
  Placement = pos=(0,0,1.5) rot=(0,0,1;0rad)
  sketch-geometry (4):
    g0: Circle CenterX=66.3968 CenterY=15.8671 CenterZ=0 NormalX=0 NormalY=0 NormalZ=1 AngleXU=0 Radius=4
    g1: Circle CenterX=81.3425 CenterY=-15.1265 CenterZ=0 NormalX=0 NormalY=0 NormalZ=1 AngleXU=0 Radius=4
    g2: Circle CenterX=66.3968 CenterY=15.8671 CenterZ=0 NormalX=0 NormalY=0 NormalZ=1 AngleXU=0 Radius=2
    g3: Circle CenterX=81.3425 CenterY=-15.1265 CenterZ=0 NormalX=0 NormalY=0 NormalZ=1 AngleXU=0 Radius=2
  constraints (6):
    c: Diameter(g0) = 8
    c: Diameter(g1) = 8
    c: Diameter(g2) = 4
    c: Coincident(g2,g0)
    c: Diameter(g3) = 4
    c: Coincident(g3,g1)
FEATURE [PartDesign::Pad] Pad041
  BaseFeature = -> LinearPattern001
  Direction = (0,0,1)
  Length = 3.5
  Length2 = 10
  Profile = -> Sketch102
  ReferenceAxis = -> Sketch102 [N_Axis]
  Refine = true
  Suppressed = false
  Type = 0
FEATURE [PartDesign::Body] Body011  label="MainArmCover"
  AllowCompound = false
  Group = -> [Sketch098,Pad039,Thickness001,Sketch099,Pocket045,Sketch100,Pad040,LinearPattern001,Sketch102,Pad041]
  Origin = -> Origin018
  Placement = pos=(5,0,-20) rot=(0,0,1;0rad)
  Tip = -> Pad041
COMPONENT P17 — geometry summary ("PCB_Arm012"; no construction recipe available for this part):
  bounding box: 40.0 x 35.0 x 8.9 mm
  tessellated surface: 15,912 triangles
  volume: 3121 mm^3 (25% of its bounding box)
PROVENANCE & LICENSES
A FreeCAD (.FCStd) document from a public repository crawl; recipes are the document's own serialized feature recipes (and, for linked parts, companion documents' recipes).
License: as declared in the source repository (recorded in the dataset sidecar).
